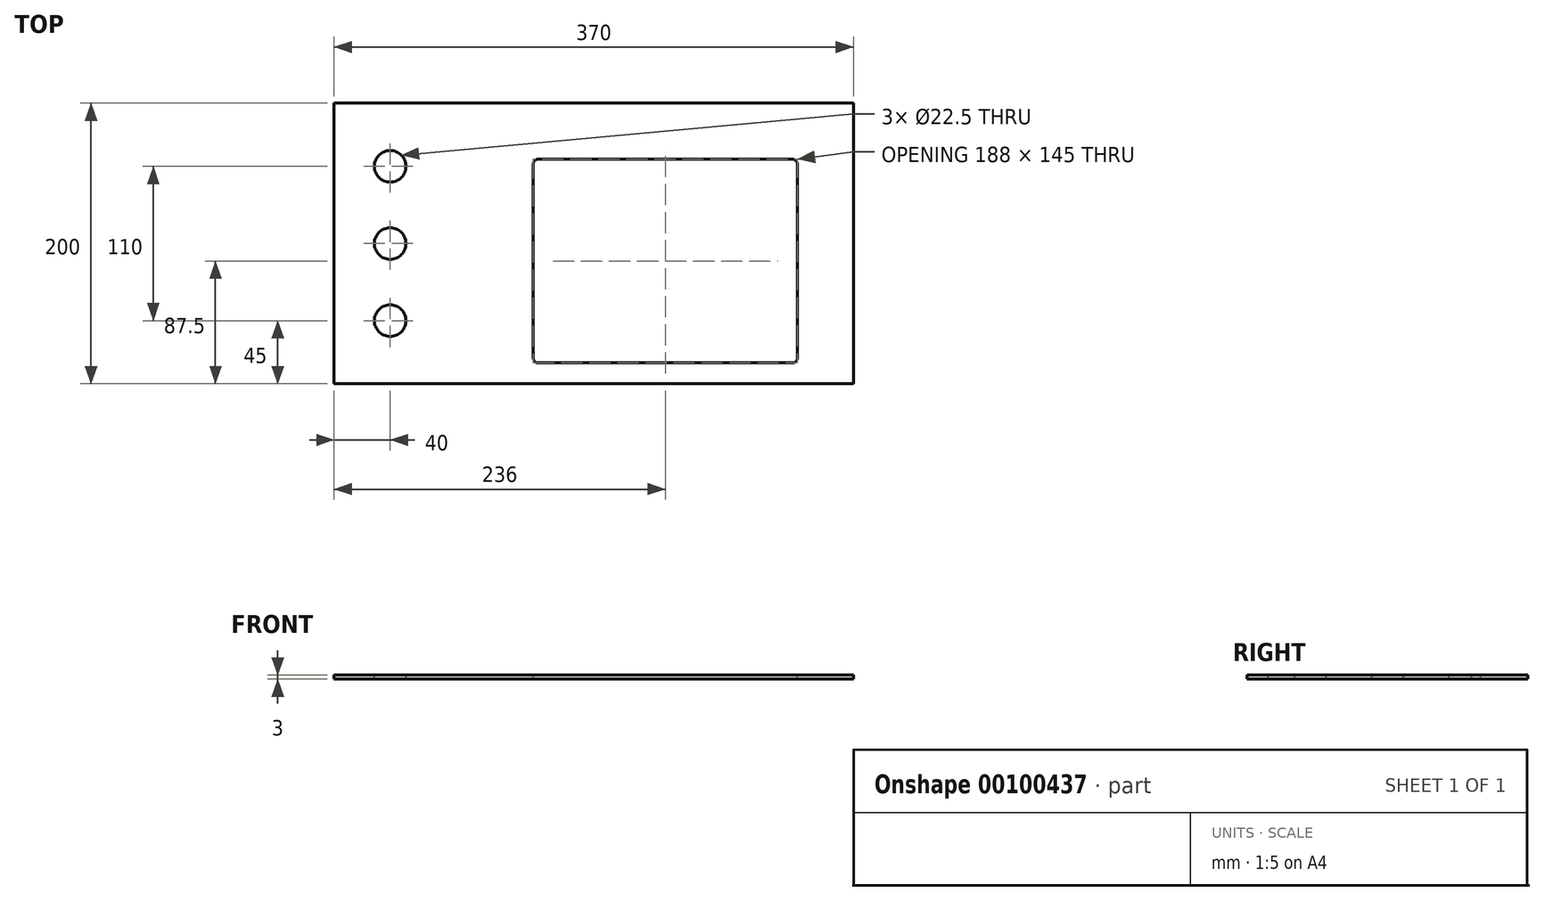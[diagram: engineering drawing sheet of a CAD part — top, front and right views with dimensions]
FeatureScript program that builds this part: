
annotation { "Feature Type Name" : "Feature", "Feature Type Description" : "" }
export const myFeature = defineFeature(function(context is Context, id is Id, definition is map)
    precondition{}
    {
        {
            var Q0;
            Q0=qCreatedBy(makeId("Top.planeOp"),FACE);
            var sketch = newSketch(context, id + "F0", { "sketchPlane" : qUnion([Q0])});
            skLineSegment(sketch, "E0.bottom", {"start": v(-185, 100) * mm, "end": v(185, 100) * mm});
            skLineSegment(sketch, "E0.top", {"start": v(-185, -100) * mm, "end": v(185, -100) * mm});
            skLineSegment(sketch, "E0.left", {"start": v(-185, 100) * mm, "end": v(-185, -100) * mm});
            skLineSegment(sketch, "E0.right", {"start": v(185, 100) * mm, "end": v(185, -100) * mm});
            skPoint(sketch, "E0.middle", {"position": v(0, 0) * mm});
            skLineSegment(sketch, "E1.bottom", {"start": v(142, -85) * mm, "end": v(-40, -85) * mm});
            skLineSegment(sketch, "E1.top", {"start": v(142, 60) * mm, "end": v(-40, 60) * mm});
            skLineSegment(sketch, "E1.left", {"start": v(145, -82) * mm, "end": v(145, 57) * mm});
            skLineSegment(sketch, "E1.right", {"start": v(-43, -82) * mm, "end": v(-43, 57) * mm});
            skPoint(sketch, "E2.visualSharp", {"position": v(145, -85) * mm});
            skArc(sketch, "E2.filletArc", {"start": v(142, -85) * mm, "mid": v(144.12, -84.12) * mm, "end": v(145, -82) * mm});
            skPoint(sketch, "E3.visualSharp", {"position": v(-43, -85) * mm});
            skArc(sketch, "E3.filletArc", {"start": v(-43, -82) * mm, "mid": v(-42.12, -84.12) * mm, "end": v(-40, -85) * mm});
            skPoint(sketch, "E4.visualSharp", {"position": v(-43, 60) * mm});
            skArc(sketch, "E4.filletArc", {"start": v(-40, 60) * mm, "mid": v(-42.12, 59.12) * mm, "end": v(-43, 57) * mm});
            skPoint(sketch, "E5.visualSharp", {"position": v(145, 60) * mm});
            skArc(sketch, "E5.filletArc", {"start": v(145, 57) * mm, "mid": v(144.12, 59.12) * mm, "end": v(142, 60) * mm});
            skSolve(sketch);
        }
        {
            var Q0;
            Q0=makeQuery(id+"F0.imprint","IMPRINT",FACE,{"disambiguationData":[TD([[makeQuery(id+"F0.imprint","IMPRINT",EDGE,{"derivedFrom":sQuery(id+"F0.wireOp",EDGE,"E0.bottom")}),-1.0]])]});
            extrude(context, id + "F1", {"entities" : qUnion([Q0]), "oppositeDirection" : true, "depth" : 3 * mm});
        }
        {
            var Q0;
            Q0=qCreatedBy(makeId("Top.planeOp"),FACE);
            var sketch = newSketch(context, id + "F2", { "sketchPlane" : qUnion([Q0])});
            skLineSegment(sketch, "E6", {"start": v(-145, -55) * mm, "end": v(-145, 55) * mm, "construction": true});
            skCircle(sketch, "E7", {"center": v(-145, -55) * mm, "radius": 11.25 * mm});
            skCircle(sketch, "E8", {"center": v(-145, 0) * mm, "radius": 11.25 * mm});
            skCircle(sketch, "E9", {"center": v(-145, 55) * mm, "radius": 11.25 * mm});
            skSolve(sketch);
        }
        {
            var Q0;
            Q0=makeQuery(id+"F2.imprint","IMPRINT",FACE,{"disambiguationData":[TD([[makeQuery(id+"F2.imprint","IMPRINT",EDGE,{"derivedFrom":sQuery(id+"F2.wireOp",EDGE,"E7")}),1.0]])]});
            var Q1;
            Q1=makeQuery(id+"F2.imprint","IMPRINT",FACE,{"disambiguationData":[TD([[makeQuery(id+"F2.imprint","IMPRINT",EDGE,{"derivedFrom":sQuery(id+"F2.wireOp",EDGE,"E8")}),1.0]])]});
            var Q2;
            Q2=makeQuery(id+"F2.imprint","IMPRINT",FACE,{"disambiguationData":[TD([[makeQuery(id+"F2.imprint","IMPRINT",EDGE,{"derivedFrom":sQuery(id+"F2.wireOp",EDGE,"E9")}),1.0]])]});
            extrude(context, id + "F3", {"entities" : qUnion([Q0, Q1, Q2]), "operationType" : NewBodyOperationType.REMOVE, "endBound" : BoundingType.THROUGH_ALL, "oppositeDirection" : true, "depth" : 25 * mm});
        }
    });
